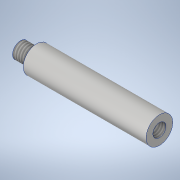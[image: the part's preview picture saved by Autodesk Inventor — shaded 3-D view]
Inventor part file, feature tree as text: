
AUTODESK INVENTOR PART (.ipt)
format: ipt  version: 2020 (Build 240168000, 168)  size: 130,048 bytes
history: native  units: mm
features: sketch x2, revolve x1, hole x1, thread x1
ambient origin geometry x8: Origin, YZ Plane, XZ Plane, XY Plane, X Axis, Y Axis, Z Axis, Center Point
bodies: Volumenkörper1 (feature_tree)
feature tree (5):
  revolve  "Umdrehung1"
  hole  "Bohrung1"  [1 undecoded]
  thread  "Gewinde1"  [1 undecoded]
  sketch  "Skizze1"  dims[d1=6.0mm d2=10.0mm d3=6.0mm]
  sketch  "Skizze2"  dims[d4=90.0deg d5=4.917mm d6=9.0mm d7=4.0mm d8=2.0mm d9=90.0deg d10=13.0mm d11=20.594885mm d12=10.0mm d13=0.0mm d18=52.0mm]
note: 2 required parameter values undecoded (feature->parameter linkage not recoverable at this tier; creation-order binding heuristic only, values carry confidence <= 0.55)
